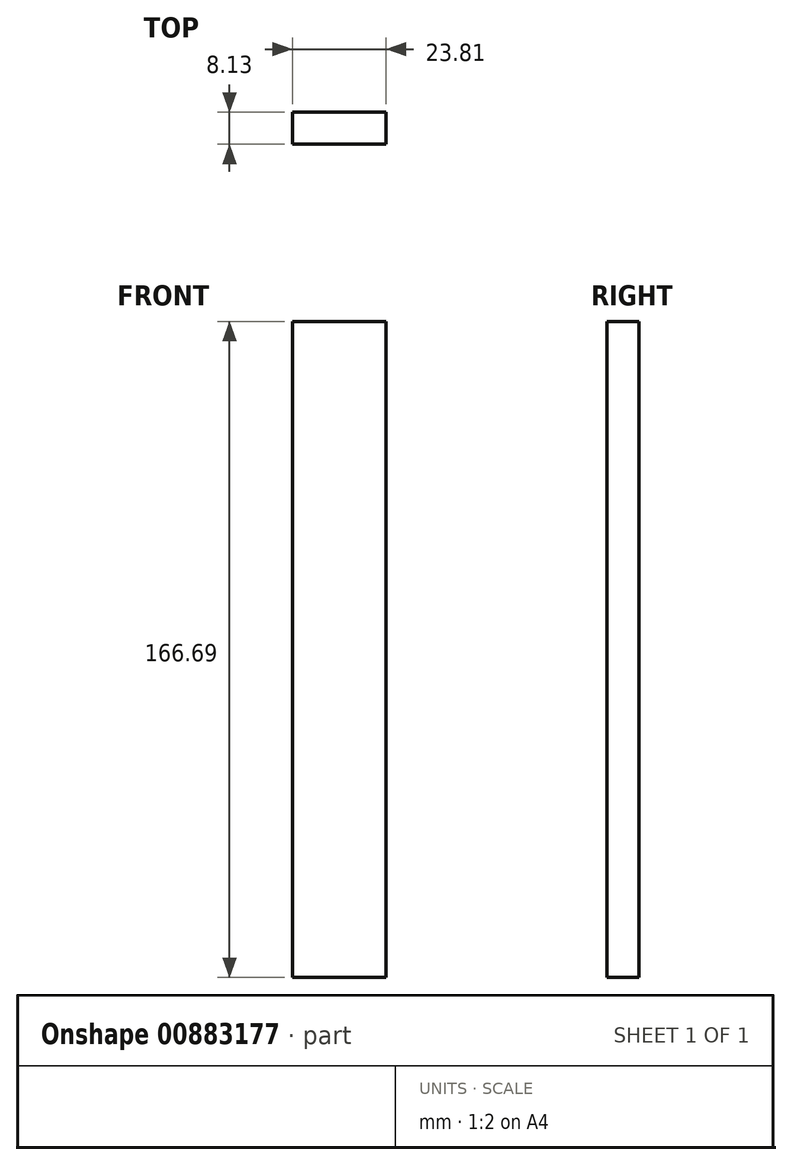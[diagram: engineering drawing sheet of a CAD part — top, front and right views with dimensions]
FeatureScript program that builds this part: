
annotation { "Feature Type Name" : "Feature", "Feature Type Description" : "" }
export const myFeature = defineFeature(function(context is Context, id is Id, definition is map)
    precondition{}
    {
        {
            var Q0;
            Q0=qCreatedBy(makeId("Front.planeOp"),FACE);
            var sketch = newSketch(context, id + "F0", { "sketchPlane" : qUnion([Q0])});
            skLineSegment(sketch, "E0.bottom", {"start": v(-52.21, 133.07) * mm, "end": v(-28.4, 133.07) * mm});
            skLineSegment(sketch, "E0.top", {"start": v(-52.21, -33.62) * mm, "end": v(-28.4, -33.62) * mm});
            skLineSegment(sketch, "E0.left", {"start": v(-52.21, 133.07) * mm, "end": v(-52.21, -33.62) * mm});
            skLineSegment(sketch, "E0.right", {"start": v(-28.4, 133.07) * mm, "end": v(-28.4, -33.62) * mm});
            skSolve(sketch);
        }
        {
            var Q0;
            Q0=makeQuery(id+"F0.imprint","IMPRINT",FACE,{"disambiguationData":[TD([[makeQuery(id+"F0.imprint","IMPRINT",EDGE,{"derivedFrom":sQuery(id+"F0.wireOp",EDGE,"E0.bottom")}),-1.0]])]});
            extrude(context, id + "F1", {"entities" : qUnion([Q0]), "depth" : 8.13 * mm, "offsetDistance" : 25.4 * mm});
        }
    });
